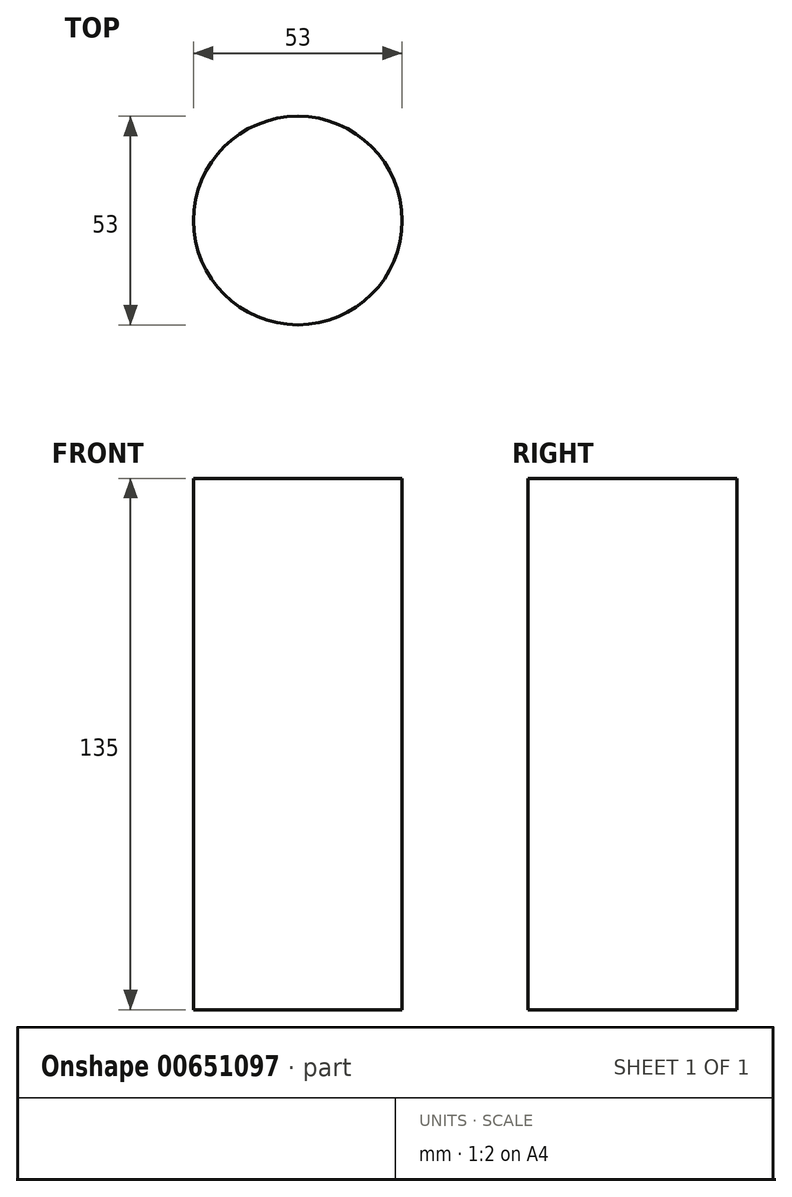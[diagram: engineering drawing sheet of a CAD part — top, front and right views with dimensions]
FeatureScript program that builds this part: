
annotation { "Feature Type Name" : "Feature", "Feature Type Description" : "" }
export const myFeature = defineFeature(function(context is Context, id is Id, definition is map)
    precondition{}
    {
        {
            var Q0;
            Q0=qCreatedBy(makeId("Top.planeOp"),FACE);
            var sketch = newSketch(context, id + "F0", { "sketchPlane" : qUnion([Q0])});
            skCircle(sketch, "E0", {"center": v(0, 0) * mm, "radius": 26.5 * mm});
            skSolve(sketch);
        }
        {
            var Q0;
            Q0 = qSketchRegion(id + "F0", true);
            extrude(context, id + "F1", {"entities" : qUnion([Q0]), "depth" : 135 * mm, "offsetDistance" : 25 * mm});
        }
    });
